# Revit family: РИДАН_Термоэлектрические приводы TWA-KR
name_source: partatom
category: Оборудование
units: mm (PartAtom-declared; Revit-internal decimal feet)

## family parameters
Всегда вертикально = Да
Классификация = Нет
На основе рабочей плоскости = Нет
Общий = Нет
При загрузке вырезать с полостями = Нет
Размер круглого соединителя = Использовать диаметр
Тип детали = Нормальный
Точка расчета площади = Нет

## types (2) — shared parameters
ADSK_Версия Revit = 2019
ADSK_Версия семейства = 1.0
ADSK_Единица измерения = шт.
ADSK_Завод-изготовитель = ООО «Ридан-Трейд»
ADSK_Классификация нагрузок = Прочее
ADSK_Количество = 1
ADSK_Коэффициент мощности = 1
ADSK_Напряжение = 24 В
ADSK_Полная мощность = 2 В·А
zero-valued in all types: ADSK_Масса

## per-type parameters (varying)
| type | ADSK_Код изделия | ADSK_Марка | ADSK_Наименование |
| TWA-KR привод, 230V, NC | 088H3142R | TWA-KR, 230V, NC | TWA-KR привод, 230V, NC норм. закрытый, соединение М30х1.5 |
| TWA-KR привод, 230V, NO | 088H3143R | TWA-KR, 230V, NO | TWA-KR привод, 230V, NO норм. открытый, соединение М30х1.5 |
